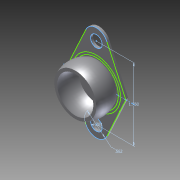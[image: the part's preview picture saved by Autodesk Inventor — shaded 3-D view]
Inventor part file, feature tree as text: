
AUTODESK INVENTOR PART (.ipt)
format: ipt  version: 2014 (Build 180170000, 170)  size: 200,704 bytes
history: native  units: in
note: dims shown in document units (in); Inventor stores cm internally (conversion verified against a paired STEP export)
features: sketch x4, extrude x2, revolve x2, mirror x1, projected_geometry x1
ambient origin geometry x8: Origin, YZ Plane, XZ Plane, XY Plane, X Axis, Y Axis, Z Axis, Center Point
bodies: Solid1 (feature_tree)
feature tree (10):
  sketch  "Sketch1"  dims[d0=0.281in d1=0.562in]
  extrude  "Extrusion1"  Depth=0.562in
  sketch  "Sketch2"  dims[d2=1.75in d21=0.063in d22=0.0in]
  sketch  "Sketch3"  dims[d28=0.0625in d29=0.125in]
  revolve  "Revolution2"  [1 undecoded]
  revolve  "Revolution3"  [1 undecoded]
  extrude  "Extrusion2"  TaperAngle=360.0deg  [1 undecoded]
  mirror  "Mirror1"
  projected_geometry  "Projected Loop1"
  sketch  "Sketch4"  dims[d30=360.0deg d31=360.0deg d32=1.125in d33=0.5625in d34=1.0in d35=0.0in]
note: 3 required parameter values undecoded (feature->parameter linkage not recoverable at this tier; creation-order binding heuristic only, values carry confidence <= 0.55)